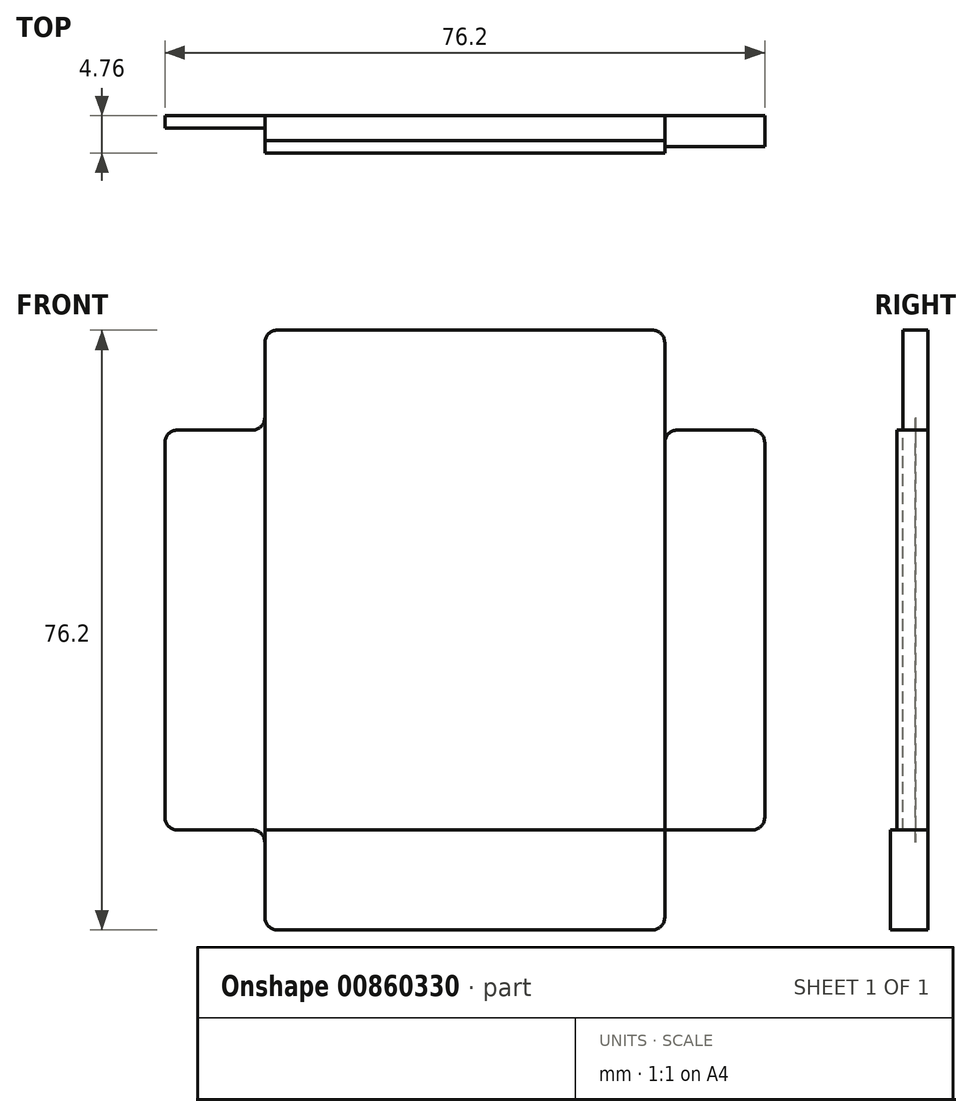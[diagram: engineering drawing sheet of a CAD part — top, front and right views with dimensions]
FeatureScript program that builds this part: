
annotation { "Feature Type Name" : "Feature", "Feature Type Description" : "" }
export const myFeature = defineFeature(function(context is Context, id is Id, definition is map)
    precondition{}
    {
        {
            var Q0;
            Q0=qCreatedBy(makeId("Front.planeOp"),FACE);
            var sketch = newSketch(context, id + "F0", { "sketchPlane" : qUnion([Q0])});
            skLineSegment(sketch, "E0.bottom", {"start": v(25.4, -38.1) * mm, "end": v(-25.4, -38.1) * mm});
            skLineSegment(sketch, "E0.top", {"start": v(25.4, 38.1) * mm, "end": v(-25.4, 38.1) * mm});
            skLineSegment(sketch, "E0.left", {"start": v(38.1, -25.4) * mm, "end": v(38.1, 25.4) * mm});
            skLineSegment(sketch, "E0.right", {"start": v(-38.1, -25.4) * mm, "end": v(-38.1, 25.4) * mm});
            skPoint(sketch, "E0.middle", {"position": v(0, 0) * mm});
            skLineSegment(sketch, "E1.bottom", {"start": v(25.4, 25.4) * mm, "end": v(-25.4, 25.4) * mm});
            skLineSegment(sketch, "E1.top", {"start": v(25.4, -25.4) * mm, "end": v(-25.4, -25.4) * mm});
            skLineSegment(sketch, "E1.left", {"start": v(25.4, 25.4) * mm, "end": v(25.4, -25.4) * mm});
            skLineSegment(sketch, "E1.right", {"start": v(-25.4, 25.4) * mm, "end": v(-25.4, -25.4) * mm});
            skLineSegment(sketch, "E2", {"start": v(-25.4, 25.4) * mm, "end": v(-25.4, 38.1) * mm});
            skLineSegment(sketch, "E3", {"start": v(25.4, 25.4) * mm, "end": v(25.4, 38.1) * mm});
            skLineSegment(sketch, "E4", {"start": v(25.4, 25.4) * mm, "end": v(38.1, 25.4) * mm});
            skLineSegment(sketch, "E5", {"start": v(25.4, -25.4) * mm, "end": v(38.1, -25.4) * mm});
            skLineSegment(sketch, "E6", {"start": v(25.4, -25.4) * mm, "end": v(25.4, -38.1) * mm});
            skLineSegment(sketch, "E7", {"start": v(-25.4, -25.4) * mm, "end": v(-25.4, -38.1) * mm});
            skLineSegment(sketch, "E8", {"start": v(-25.4, -25.4) * mm, "end": v(-38.1, -25.4) * mm});
            skLineSegment(sketch, "E9", {"start": v(-25.4, 25.4) * mm, "end": v(-38.1, 25.4) * mm});
            skPoint(sketch, "E10.orphan", {"position": v(-38.1, 38.1) * mm});
            skPoint(sketch, "E11.orphan", {"position": v(-38.1, -38.1) * mm});
            skPoint(sketch, "E12.orphan", {"position": v(38.1, -38.1) * mm});
            skPoint(sketch, "E13.orphan", {"position": v(38.1, 38.1) * mm});
            skSolve(sketch);
        }
        {
            var Q0;
            Q0=makeQuery(id+"F0.imprint","IMPRINT",FACE,{"disambiguationData":[TD([[makeQuery(id+"F0.imprint","IMPRINT",EDGE,{"derivedFrom":sQuery(id+"F0.wireOp",EDGE,"E0.top")}),1.0]])]});
            extrude(context, id + "F1", {"entities" : qUnion([Q0]), "depth" : 3.17 * mm, "offsetDistance" : 25.4 * mm});
        }
        {
            var Q0;
            Q0=makeQuery(id+"F0.imprint","IMPRINT",FACE,{"disambiguationData":[TD([[makeQuery(id+"F0.imprint","IMPRINT",EDGE,{"derivedFrom":sQuery(id+"F0.wireOp",EDGE,"E0.left")}),1.0]])]});
            extrude(context, id + "F2", {"entities" : qUnion([Q0]), "operationType" : NewBodyOperationType.ADD, "depth" : 3.97 * mm, "offsetDistance" : 25.4 * mm});
        }
        {
            var Q0;
            Q0=makeQuery(id+"F0.imprint","IMPRINT",FACE,{"disambiguationData":[TD([[makeQuery(id+"F0.imprint","IMPRINT",EDGE,{"derivedFrom":sQuery(id+"F0.wireOp",EDGE,"E0.bottom")}),-1.0]])]});
            extrude(context, id + "F3", {"entities" : qUnion([Q0]), "operationType" : NewBodyOperationType.ADD, "depth" : 4.76 * mm, "offsetDistance" : 25.4 * mm});
        }
        {
            var Q0;
            Q0=makeQuery(id+"F0.imprint","IMPRINT",FACE,{"disambiguationData":[TD([[makeQuery(id+"F0.imprint","IMPRINT",EDGE,{"derivedFrom":sQuery(id+"F0.wireOp",EDGE,"E0.right")}),-1.0]])]});
            extrude(context, id + "F4", {"entities" : qUnion([Q0]), "operationType" : NewBodyOperationType.ADD, "depth" : 1.59 * mm, "offsetDistance" : 25.4 * mm});
        }
        {
            var Q0;
            Q0=makeQuery(id+"F0.imprint","IMPRINT",FACE,{"disambiguationData":[TD([[makeQuery(id+"F0.imprint","IMPRINT",EDGE,{"derivedFrom":sQuery(id+"F0.wireOp",EDGE,"E1.bottom")}),1.0]])]});
            extrude(context, id + "F5", {"entities" : qUnion([Q0]), "operationType" : NewBodyOperationType.ADD, "depth" : 3.17 * mm, "offsetDistance" : 25.4 * mm});
        }
        {
            var Q0;
            Q0=makeQuery(id+"F3.opExtrude","SWEPT_EDGE",EDGE,{"disambiguationData":[OSD([sQuery(id+"F0.wireOp",EDGE,"E0.bottom"),sQuery(id+"F0.wireOp",EDGE,"E7")])]});
            var Q1;
            Q1=makeQuery(id+"F3.opExtrude","SWEPT_EDGE",EDGE,{"disambiguationData":[OSD([sQuery(id+"F0.wireOp",EDGE,"E0.bottom"),sQuery(id+"F0.wireOp",EDGE,"E6")])]});
            var Q2;
            Q2=makeQuery(id+"F2.opExtrude","SWEPT_EDGE",EDGE,{"disambiguationData":[OSD([sQuery(id+"F0.wireOp",EDGE,"E0.left"),sQuery(id+"F0.wireOp",EDGE,"E5")])]});
            var Q3;
            Q3=makeQuery(id+"F4.opExtrude","SWEPT_EDGE",EDGE,{"disambiguationData":[OSD([sQuery(id+"F0.wireOp",EDGE,"E0.right"),sQuery(id+"F0.wireOp",EDGE,"E8")])]});
            var Q4;
            Q4=makeQuery(id+"F4.opExtrude","SWEPT_EDGE",EDGE,{"disambiguationData":[OSD([sQuery(id+"F0.wireOp",EDGE,"E0.right"),sQuery(id+"F0.wireOp",EDGE,"E9")])]});
            var Q5;
            Q5=makeQuery(id+"F1.opExtrude","SWEPT_EDGE",EDGE,{"disambiguationData":[OSD([sQuery(id+"F0.wireOp",EDGE,"E1.bottom"),sQuery(id+"F0.wireOp",EDGE,"E1.right"),sQuery(id+"F0.wireOp",EDGE,"E2"),sQuery(id+"F0.wireOp",EDGE,"E9")])]});
            var Q6;
            Q6=makeQuery(id+"F1.opExtrude","SWEPT_EDGE",EDGE,{"disambiguationData":[OSD([sQuery(id+"F0.wireOp",EDGE,"E0.top"),sQuery(id+"F0.wireOp",EDGE,"E2")])]});
            var Q7;
            Q7=makeQuery(id+"F1.opExtrude","SWEPT_EDGE",EDGE,{"disambiguationData":[OSD([sQuery(id+"F0.wireOp",EDGE,"E0.top"),sQuery(id+"F0.wireOp",EDGE,"E3")])]});
            var Q8;
            {var subQ0=sQuery(id+"F0.wireOp",EDGE,"E4");var subQ1=sQuery(id+"F0.wireOp",EDGE,"E1.left");Q8=makeQuery(id+"F5.boolean.opBoolean","SPLIT",EDGE,{"disambiguationData":[TD([makeQuery(id+"F2.opExtrude","CAP_FACE",FACE,{"disambiguationData":[OSD([sQuery(id+"F0.wireOp",EDGE,"E0.left"),subQ1,subQ0,sQuery(id+"F0.wireOp",EDGE,"E5")])],"isStart":true})])],"derivedFrom":makeQuery(id+"F2.opExtrude","SWEPT_EDGE",EDGE,{"disambiguationData":[OSD([sQuery(id+"F0.wireOp",EDGE,"E1.bottom"),subQ1,sQuery(id+"F0.wireOp",EDGE,"E3"),subQ0])]})});}
            var Q9;
            Q9=makeQuery(id+"F2.opExtrude","SWEPT_EDGE",EDGE,{"disambiguationData":[OSD([sQuery(id+"F0.wireOp",EDGE,"E0.left"),sQuery(id+"F0.wireOp",EDGE,"E4")])]});
            var Q10;
            Q10=makeQuery(id+"F5.boolean.opBoolean","TWEAK_EDGE",EDGE,{"derivedFrom":[makeQuery(id+"F1.opExtrude","SWEPT_FACE",FACE,{"disambiguationData":[OSD([sQuery(id+"F0.wireOp",EDGE,"E3")])]}),makeQuery(id+"F3.opExtrude","SWEPT_FACE",FACE,{"disambiguationData":[OSD([sQuery(id+"F0.wireOp",EDGE,"E6")])]}),makeQuery(id+"F5.opExtrude","SWEPT_FACE",FACE,{"disambiguationData":[OSD([sQuery(id+"F0.wireOp",EDGE,"E1.left")])]})]});
            var Q11;
            {var subQ0=sQuery(id+"F0.wireOp",EDGE,"E1.top");var subQ1=sQuery(id+"F0.wireOp",EDGE,"E8");var subQ2=sQuery(id+"F0.wireOp",EDGE,"E7");var subQ3=sQuery(id+"F0.wireOp",EDGE,"E1.right");Q11=makeQuery(id+"F5.boolean.opBoolean","SPLIT",EDGE,{"disambiguationData":[topologyDisambiguationEdgeConnected([makeQuery(id+"F4.opExtrude","SWEPT_FACE",FACE,{"disambiguationData":[OSD([subQ1])]})])],"derivedFrom":makeQuery(id+"F3.opExtrude","SWEPT_EDGE",EDGE,{"disambiguationData":[OSD([subQ0,subQ3,subQ2,subQ1])]})});}
            var Q12;
            Q12=makeQuery(id+"F5.opExtrude","CAP_EDGE",EDGE,{"disambiguationData":[OSD([sQuery(id+"F0.wireOp",EDGE,"E1.top")])],"isStart":false});
            fillet(context, id + "F6", {"entities" : qUnion([Q0, Q1, Q2, Q3, Q4, Q5, Q6, Q7, Q8, Q9, Q10, Q11, Q12]), "radius" : 1.59 * mm, "tangentPropagation" : true, "allowEdgeOverflow" : false});
        }
    });
